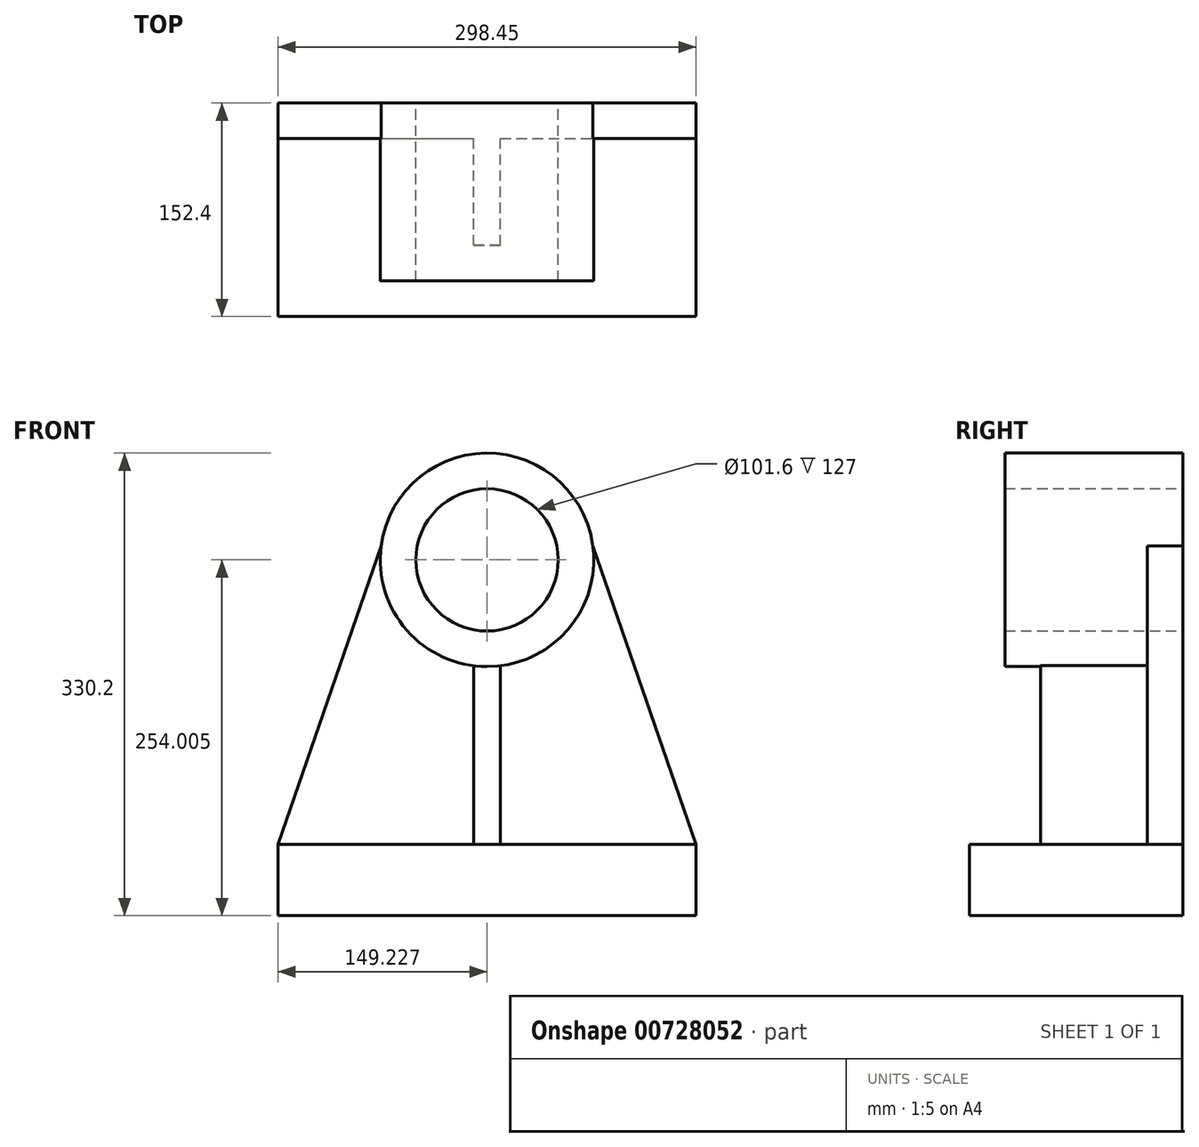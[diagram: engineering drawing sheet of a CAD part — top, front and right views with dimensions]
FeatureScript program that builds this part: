
annotation { "Feature Type Name" : "Feature", "Feature Type Description" : "" }
export const myFeature = defineFeature(function(context is Context, id is Id, definition is map)
    precondition{}
    {
        {
            var Q0;
            Q0=qCreatedBy(makeId("Front.planeOp"),FACE);
            var sketch = newSketch(context, id + "F0", { "sketchPlane" : qUnion([Q0])});
            skCircle(sketch, "E0", {"center": v(-51.77, -20.54) * mm, "radius": 76.2 * mm});
            skCircle(sketch, "E1", {"center": v(-51.77, -20.54) * mm, "radius": 50.8 * mm});
            skLineSegment(sketch, "E2", {"start": v(-42.25, -96.14) * mm, "end": v(-42.25, -223.74) * mm});
            skLineSegment(sketch, "E3", {"start": v(-42.25, -223.74) * mm, "end": v(-61.3, -223.74) * mm});
            skLineSegment(sketch, "E4", {"start": v(-61.3, -223.74) * mm, "end": v(-61.3, -96.14) * mm});
            skLineSegment(sketch, "E5", {"start": v(-42.25, -223.74) * mm, "end": v(97.45, -223.74) * mm});
            skLineSegment(sketch, "E6", {"start": v(97.45, -223.74) * mm, "end": v(97.45, -274.54) * mm});
            skLineSegment(sketch, "E7", {"start": v(97.45, -274.54) * mm, "end": v(-201, -274.54) * mm});
            skLineSegment(sketch, "E8", {"start": v(-201, -274.54) * mm, "end": v(-201, -223.74) * mm});
            skLineSegment(sketch, "E9", {"start": v(-201, -223.74) * mm, "end": v(-61.3, -223.74) * mm});
            skLineSegment(sketch, "E10", {"start": v(-201, -223.74) * mm, "end": v(-127.33, -10.68) * mm});
            skLineSegment(sketch, "E11", {"start": v(97.45, -223.74) * mm, "end": v(23.79, -10.68) * mm});
            skSolve(sketch);
        }
        {
            var Q0;
            Q0=makeQuery(id+"F0.imprint","IMPRINT",FACE,{"disambiguationData":[TD([[makeQuery(id+"F0.imprint","IMPRINT",EDGE,{"derivedFrom":sQuery(id+"F0.wireOp",EDGE,"E1")}),-1.0]])]});
            extrude(context, id + "F1", {"entities" : qUnion([Q0]), "depth" : 127 * mm, "offsetDistance" : 25.4 * mm});
        }
        {
            var Q0;
            {var subQ0=sQuery(id+"F0.wireOp",EDGE,"E2");Q0=makeQuery(id+"F0.imprint","IMPRINT",FACE,{"disambiguationData":[TD([[makeQuery(id+"F0.imprint","IMPRINT",EDGE,{"derivedFrom":subQ0}),-1.0]])]});}
            extrude(context, id + "F2", {"entities" : qUnion([Q0]), "operationType" : NewBodyOperationType.ADD, "depth" : 101.6 * mm, "offsetDistance" : 25.4 * mm});
        }
        {
            var Q0;
            Q0=makeQuery(id+"F0.imprint","IMPRINT",FACE,{"disambiguationData":[TD([[makeQuery(id+"F0.imprint","IMPRINT",EDGE,{"derivedFrom":sQuery(id+"F0.wireOp",EDGE,"E3")}),1.0]])]});
            extrude(context, id + "F3", {"entities" : qUnion([Q0]), "operationType" : NewBodyOperationType.ADD, "depth" : 152.4 * mm, "offsetDistance" : 25.4 * mm});
        }
        {
            var Q0;
            {var subQ0=sQuery(id+"F0.wireOp",EDGE,"E4");Q0=makeQuery(id+"F0.imprint","IMPRINT",FACE,{"disambiguationData":[TD([[makeQuery(id+"F0.imprint","IMPRINT",EDGE,{"derivedFrom":subQ0}),1.0]])]});}
            var Q1;
            {var subQ0=sQuery(id+"F0.wireOp",EDGE,"E2");Q1=makeQuery(id+"F0.imprint","IMPRINT",FACE,{"disambiguationData":[TD([[makeQuery(id+"F0.imprint","IMPRINT",EDGE,{"derivedFrom":subQ0}),1.0]])]});}
            extrude(context, id + "F4", {"entities" : qUnion([Q0, Q1]), "operationType" : NewBodyOperationType.ADD, "depth" : 25.4 * mm, "offsetDistance" : 25.4 * mm});
        }
    });
